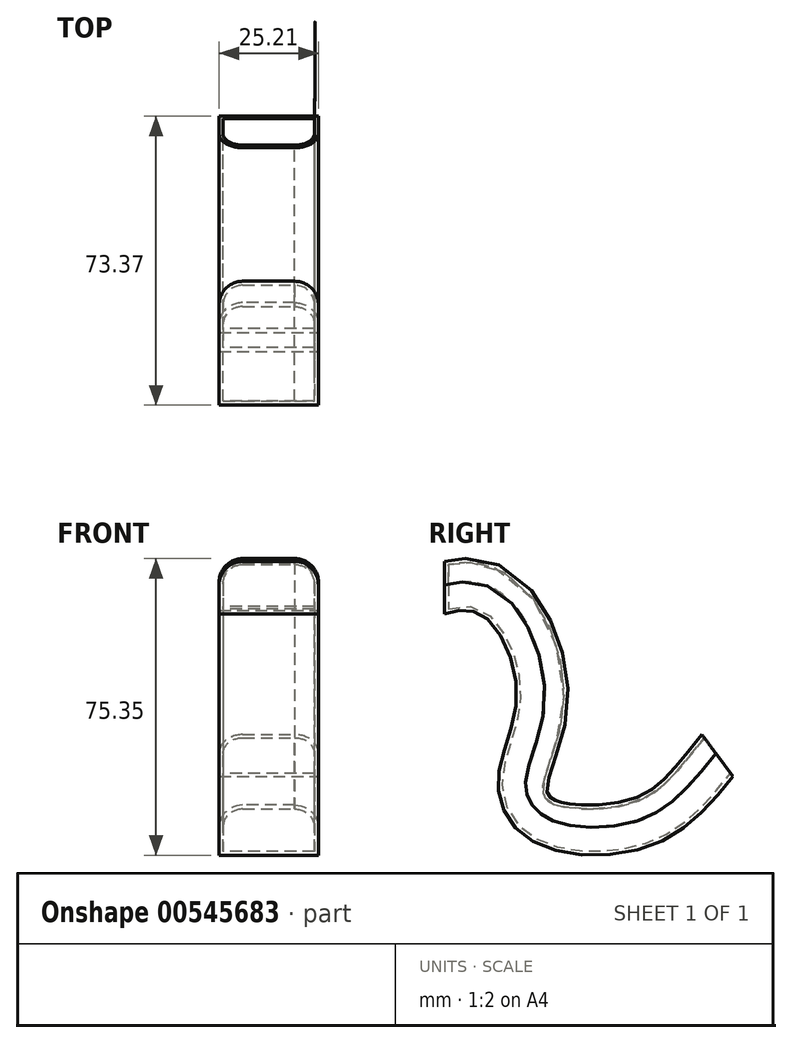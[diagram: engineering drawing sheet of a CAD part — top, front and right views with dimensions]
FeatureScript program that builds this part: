
annotation { "Feature Type Name" : "Feature", "Feature Type Description" : "" }
export const myFeature = defineFeature(function(context is Context, id is Id, definition is map)
    precondition{}
    {
        {
            var Q0;
            Q0=qCreatedBy(makeId("Front.planeOp"),FACE);
            var sketch = newSketch(context, id + "F0", { "sketchPlane" : qUnion([Q0])});
            skLineSegment(sketch, "E0.bottom", {"start": v(-7.6, 38.53) * mm, "end": v(5.61, 38.53) * mm});
            skLineSegment(sketch, "E0.top", {"start": v(-13.6, 25.21) * mm, "end": v(11.61, 25.21) * mm});
            skLineSegment(sketch, "E0.left", {"start": v(-13.6, 32.53) * mm, "end": v(-13.6, 25.21) * mm});
            skLineSegment(sketch, "E0.right", {"start": v(11.61, 32.53) * mm, "end": v(11.61, 25.21) * mm});
            skPoint(sketch, "E1.visualSharp", {"position": v(-13.6, 38.53) * mm});
            skArc(sketch, "E1.filletArc", {"start": v(-7.6, 38.53) * mm, "mid": v(-11.84, 36.77) * mm, "end": v(-13.6, 32.53) * mm});
            skPoint(sketch, "E2.visualSharp", {"position": v(11.61, 38.53) * mm});
            skArc(sketch, "E2.filletArc", {"start": v(11.61, 32.53) * mm, "mid": v(9.86, 36.77) * mm, "end": v(5.61, 38.53) * mm});
            skSolve(sketch);
        }
        {
            var Q0;
            Q0=qCreatedBy(makeId("Right.planeOp"),FACE);
            var sketch = newSketch(context, id + "F1", { "sketchPlane" : qUnion([Q0])});
            skFitSpline(sketch, "E3", {"points": [v(0, 25.21) * mm, v(9.63, 24.93) * mm, v(18.41, 4.53) * mm, v(13.6, -17.28) * mm, v(22.95, -32.86) * mm, v(53.82, -33.14) * mm, v(73.37, -16.15) * mm], "startDerivative": vector(86.91, 22.02) * mm, "endDerivative": vector(88.16, 108.5) * mm});
            skSolve(sketch);
        }
        {
            var Q0;
            Q0=makeQuery(id+"F0.imprint","IMPRINT",FACE,{"disambiguationData":[TD([[makeQuery(id+"F0.imprint","IMPRINT",EDGE,{"derivedFrom":sQuery(id+"F0.wireOp",EDGE,"E0.bottom")}),-1.0]])]});
            var Q1;
            Q1=sQuery(id+"F1.wireOp",EDGE,"E3");
            sweep(context, id + "F2", {"profiles" : qUnion([Q0]), "path" : qUnion([Q1])});
        }
        {
            var Q0;
            Q0=makeQuery(id+"F2.opSweep","CAP_FACE",FACE,{"disambiguationData":[OSD([sQuery(id+"F0.wireOp",EDGE,"E0.bottom"),sQuery(id+"F0.wireOp",EDGE,"E0.top"),sQuery(id+"F0.wireOp",EDGE,"E0.left"),sQuery(id+"F0.wireOp",EDGE,"E0.right"),sQuery(id+"F0.wireOp",EDGE,"E1.filletArc"),sQuery(id+"F0.wireOp",EDGE,"E2.filletArc"),sQuery(id+"F1.wireOp",VERTEX,"E3.end")])],"isStart":false});
            shell(context, id + "F3", {"entities" : qUnion([Q0]), "thickness" : 1 * mm});
        }
    });
